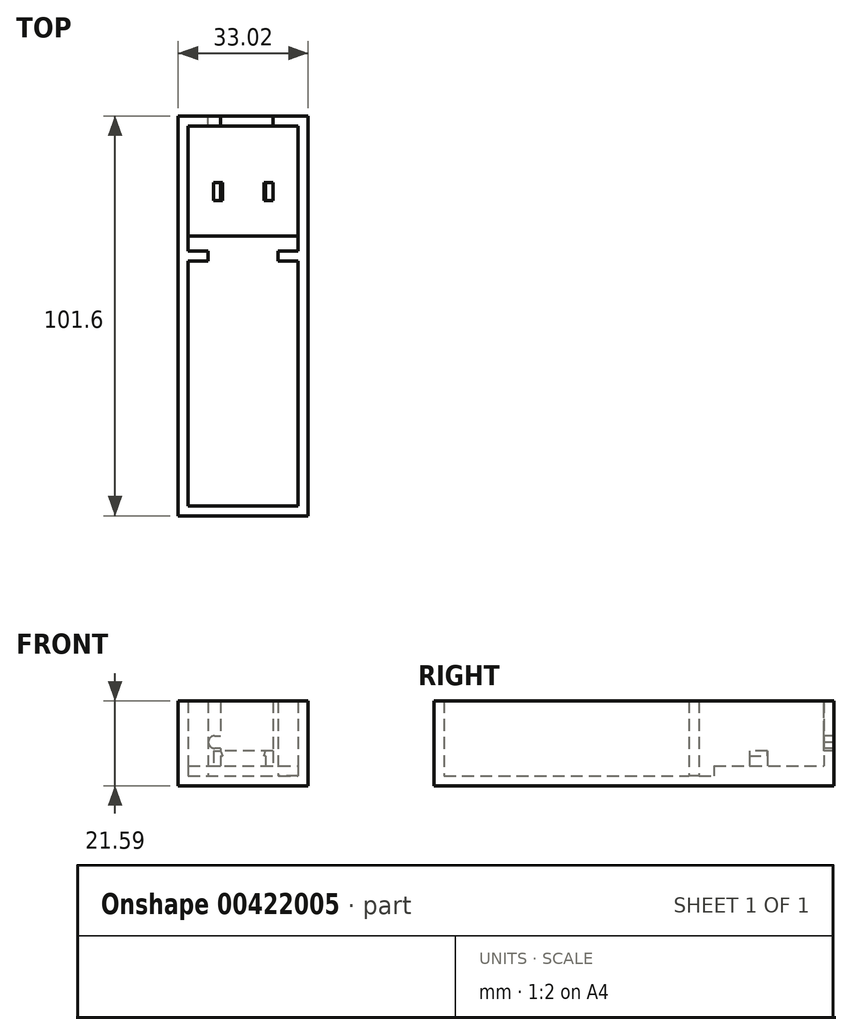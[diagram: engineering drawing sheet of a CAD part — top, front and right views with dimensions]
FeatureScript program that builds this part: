
annotation { "Feature Type Name" : "Feature", "Feature Type Description" : "" }
export const myFeature = defineFeature(function(context is Context, id is Id, definition is map)
    precondition{}
    {
        {
            var Q0;
            Q0=qCreatedBy(makeId("Top.planeOp"),FACE);
            var sketch = newSketch(context, id + "F0", { "sketchPlane" : qUnion([Q0])});
            skLineSegment(sketch, "E0.bottom", {"start": v(0, 0) * mm, "end": v(33.02, 0) * mm});
            skLineSegment(sketch, "E0.top", {"start": v(0, 101.6) * mm, "end": v(33.02, 101.6) * mm});
            skLineSegment(sketch, "E0.left", {"start": v(0, 0) * mm, "end": v(0, 101.6) * mm});
            skLineSegment(sketch, "E0.right", {"start": v(33.02, 0) * mm, "end": v(33.02, 101.6) * mm});
            skSolve(sketch);
        }
        {
            var Q0;
            Q0 = qSketchRegion(id + "F0", true);
            var Q1;
            Q1=makeQuery(id+"F0.imprint","IMPRINT",FACE,{"disambiguationData":[TD([[makeQuery(id+"F0.imprint","IMPRINT",EDGE,{"derivedFrom":sQuery(id+"F0.wireOp",EDGE,"E0.bottom")}),1.0]])]});
            extrude(context, id + "F1", {"entities" : qUnion([Q0, Q1]), "depth" : 2.54 * mm});
        }
        {
            var Q0;
            Q0=makeQuery(id+"F1.opExtrude","CAP_FACE",FACE,{"disambiguationData":[OSD([sQuery(id+"F0.wireOp",EDGE,"E0.bottom"),sQuery(id+"F0.wireOp",EDGE,"E0.top"),sQuery(id+"F0.wireOp",EDGE,"E0.left"),sQuery(id+"F0.wireOp",EDGE,"E0.right")])],"isStart":false});
            var sketch = newSketch(context, id + "F2", { "sketchPlane" : qUnion([Q0])});
            skLineSegment(sketch, "E1.bottom", {"start": v(2.54, 2.54) * mm, "end": v(30.48, 2.54) * mm});
            skLineSegment(sketch, "E1.top", {"start": v(2.54, 99.06) * mm, "end": v(30.48, 99.06) * mm});
            skLineSegment(sketch, "E1.left", {"start": v(2.54, 2.54) * mm, "end": v(2.54, 99.06) * mm});
            skLineSegment(sketch, "E1.right", {"start": v(30.48, 2.54) * mm, "end": v(30.48, 99.06) * mm});
            skLineSegment(sketch, "E2", {"start": v(2.54, 71.12) * mm, "end": v(30.48, 71.12) * mm});
            skLineSegment(sketch, "E3.bottom", {"start": v(22.22, 80.06) * mm, "end": v(24.05, 80.06) * mm});
            skLineSegment(sketch, "E3.top", {"start": v(22.22, 84.63) * mm, "end": v(24.05, 84.63) * mm});
            skLineSegment(sketch, "E3.left", {"start": v(22.22, 80.06) * mm, "end": v(22.22, 84.63) * mm});
            skLineSegment(sketch, "E3.right", {"start": v(24.05, 80.06) * mm, "end": v(24.05, 84.63) * mm});
            skLineSegment(sketch, "E4.bottom", {"start": v(8.97, 80.06) * mm, "end": v(10.8, 80.06) * mm});
            skLineSegment(sketch, "E4.top", {"start": v(8.97, 84.63) * mm, "end": v(10.8, 84.63) * mm});
            skLineSegment(sketch, "E4.left", {"start": v(10.8, 80.06) * mm, "end": v(10.8, 84.63) * mm});
            skLineSegment(sketch, "E4.right", {"start": v(8.97, 80.06) * mm, "end": v(8.97, 84.63) * mm});
            skLineSegment(sketch, "E5", {"start": v(16.51, 71.12) * mm, "end": v(16.5, 99.06) * mm, "construction": true});
            skLineSegment(sketch, "E6", {"start": v(22.22, 80.06) * mm, "end": v(16.5, 80.06) * mm, "construction": true});
            skLineSegment(sketch, "E7", {"start": v(16.5, 80.06) * mm, "end": v(10.8, 80.06) * mm, "construction": true});
            skLineSegment(sketch, "E8.bottom", {"start": v(2.54, 67.31) * mm, "end": v(7.62, 67.31) * mm});
            skLineSegment(sketch, "E8.top", {"start": v(2.54, 64.77) * mm, "end": v(7.62, 64.77) * mm});
            skLineSegment(sketch, "E8.left", {"start": v(2.54, 67.31) * mm, "end": v(2.54, 64.77) * mm});
            skLineSegment(sketch, "E8.right", {"start": v(7.62, 67.31) * mm, "end": v(7.62, 64.77) * mm});
            skLineSegment(sketch, "E9.bottom", {"start": v(30.48, 67.31) * mm, "end": v(25.4, 67.31) * mm});
            skLineSegment(sketch, "E9.top", {"start": v(30.48, 64.77) * mm, "end": v(25.4, 64.77) * mm});
            skLineSegment(sketch, "E9.left", {"start": v(30.48, 67.31) * mm, "end": v(30.48, 64.77) * mm});
            skLineSegment(sketch, "E9.right", {"start": v(25.4, 67.31) * mm, "end": v(25.4, 64.77) * mm});
            skSolve(sketch);
        }
        {
            var Q0;
            Q0=makeQuery(id+"F2.imprint","IMPRINT",FACE,{"disambiguationData":[TD([[makeQuery(id+"F2.imprint","IMPRINT",EDGE,{"derivedFrom":sQuery(id+"F2.wireOp",EDGE,"E1.bottom")}),-1.0]])]});
            var Q1;
            Q1=makeQuery(id+"F2.imprint","IMPRINT",FACE,{"disambiguationData":[TD([[makeQuery(id+"F2.imprint","IMPRINT",EDGE,{"derivedFrom":sQuery(id+"F2.wireOp",EDGE,"E8.bottom")}),-1.0]])]});
            var Q2;
            Q2=makeQuery(id+"F2.imprint","IMPRINT",FACE,{"disambiguationData":[TD([[makeQuery(id+"F2.imprint","IMPRINT",EDGE,{"derivedFrom":sQuery(id+"F2.wireOp",EDGE,"E9.bottom")}),1.0]])]});
            extrude(context, id + "F3", {"entities" : qUnion([Q0, Q1, Q2]), "operationType" : NewBodyOperationType.ADD, "depth" : 19.05 * mm});
        }
        {
            var Q0;
            {var subQ0=sQuery(id+"F2.wireOp",EDGE,"E1.top");Q0=makeQuery(id+"F2.imprint","IMPRINT",FACE,{"disambiguationData":[TD([[makeQuery(id+"F2.imprint","IMPRINT",EDGE,{"derivedFrom":subQ0}),-1.0]])]});}
            extrude(context, id + "F4", {"entities" : qUnion([Q0]), "operationType" : NewBodyOperationType.ADD, "depth" : 2.54 * mm});
        }
        {
            var Q0;
            Q0=makeQuery(id+"F2.imprint","IMPRINT",FACE,{"disambiguationData":[TD([[makeQuery(id+"F2.imprint","IMPRINT",EDGE,{"derivedFrom":sQuery(id+"F2.wireOp",EDGE,"E4.bottom")}),1.0]])]});
            var Q1;
            Q1=makeQuery(id+"F2.imprint","IMPRINT",FACE,{"disambiguationData":[TD([[makeQuery(id+"F2.imprint","IMPRINT",EDGE,{"derivedFrom":sQuery(id+"F2.wireOp",EDGE,"E3.bottom")}),1.0]])]});
            extrude(context, id + "F5", {"entities" : qUnion([Q0, Q1]), "operationType" : NewBodyOperationType.ADD, "depth" : 5.08 * mm});
        }
        {
            var Q0;
            Q0=makeQuery(id+"F4.opExtrude","CAP_FACE",FACE,{"disambiguationData":[OSD([sQuery(id+"F2.wireOp",EDGE,"E1.top"),sQuery(id+"F2.wireOp",EDGE,"E1.left"),sQuery(id+"F2.wireOp",EDGE,"E1.right"),sQuery(id+"F2.wireOp",EDGE,"E2"),sQuery(id+"F2.wireOp",EDGE,"E3.bottom"),sQuery(id+"F2.wireOp",EDGE,"E3.top"),sQuery(id+"F2.wireOp",EDGE,"E3.left"),sQuery(id+"F2.wireOp",EDGE,"E3.right"),sQuery(id+"F2.wireOp",EDGE,"E4.bottom"),sQuery(id+"F2.wireOp",EDGE,"E4.top"),sQuery(id+"F2.wireOp",EDGE,"E4.left"),sQuery(id+"F2.wireOp",EDGE,"E4.right")])],"isStart":false});
            var sketch = newSketch(context, id + "F6", { "sketchPlane" : qUnion([Q0])});
            skLineSegment(sketch, "E10", {"start": v(24.05, 84.63) * mm, "end": v(24.05, 99.06) * mm, "construction": true});
            skLineSegment(sketch, "E11", {"start": v(10.8, 84.63) * mm, "end": v(10.8, 99.06) * mm, "construction": true});
            skSolve(sketch);
        }
        {
            var Q0;
            Q0=makeQuery(id+"F3.opExtrude","SWEPT_FACE",FACE,{"disambiguationData":[OSD([sQuery(id+"F2.wireOp",EDGE,"E1.top")])]});
            var sketch = newSketch(context, id + "F7", { "sketchPlane" : qUnion([Q0])});
            skLineSegment(sketch, "E12.bottom", {"start": v(10.8, 8.9) * mm, "end": v(24.05, 8.9) * mm});
            skLineSegment(sketch, "E12.top", {"start": v(10.8, 21.59) * mm, "end": v(24.05, 21.59) * mm});
            skLineSegment(sketch, "E12.left", {"start": v(10.8, 8.9) * mm, "end": v(10.8, 21.59) * mm});
            skLineSegment(sketch, "E12.right", {"start": v(24.05, 8.9) * mm, "end": v(24.05, 21.59) * mm});
            skLineSegment(sketch, "E13", {"start": v(24.05, 8.9) * mm, "end": v(24.05, 5.08) * mm, "construction": true});
            skLineSegment(sketch, "E14", {"start": v(10.8, 8.9) * mm, "end": v(10.8, 5.08) * mm, "construction": true});
            skLineSegment(sketch, "E15", {"start": v(10.8, 12.7) * mm, "end": v(7.64, 12.7) * mm});
            skLineSegment(sketch, "E16", {"start": v(7.64, 12.7) * mm, "end": v(7.64, 9.53) * mm});
            skLineSegment(sketch, "E17", {"start": v(7.64, 9.53) * mm, "end": v(10.8, 9.53) * mm});
            skSolve(sketch);
        }
        {
            var Q0;
            Q0=makeQuery(id+"F7.imprint","IMPRINT",FACE,{"disambiguationData":[TD([[makeQuery(id+"F7.imprint","IMPRINT",EDGE,{"derivedFrom":sQuery(id+"F7.wireOp",EDGE,"E12.bottom")}),1.0]])]});
            var Q1;
            {var subQ0=sQuery(id+"F7.wireOp",EDGE,"E15");Q1=makeQuery(id+"F7.imprint","IMPRINT",FACE,{"disambiguationData":[TD([[makeQuery(id+"F7.imprint","IMPRINT",EDGE,{"derivedFrom":subQ0}),1.0]])]});}
            extrude(context, id + "F8", {"entities" : qUnion([Q0, Q1]), "operationType" : NewBodyOperationType.REMOVE, "oppositeDirection" : true, "depth" : 25.4 * mm});
        }
        {
            var Q0;
            Q0=makeQuery(id+"F8.boolean.opBoolean","COPY",EDGE,{"derivedFrom":makeQuery(id+"F8.opExtrude","SWEPT_EDGE",EDGE,{"disambiguationData":[OSD([sQuery(id+"F7.wireOp",EDGE,"E15"),sQuery(id+"F7.wireOp",EDGE,"E16")])]})});
            var Q1;
            Q1=makeQuery(id+"F8.boolean.opBoolean","COPY",EDGE,{"derivedFrom":makeQuery(id+"F8.opExtrude","SWEPT_EDGE",EDGE,{"disambiguationData":[OSD([sQuery(id+"F7.wireOp",EDGE,"E16"),sQuery(id+"F7.wireOp",EDGE,"E17")])]})});
            fillet(context, id + "F9", {"entities" : qUnion([Q0, Q1]), "radius" : 1.65 * mm, "tangentPropagation" : true, "allowEdgeOverflow" : false});
        }
        {
            var Q0;
            Q0=makeQuery(id+"F5.opExtrude","CAP_FACE",FACE,{"disambiguationData":[OSD([sQuery(id+"F2.wireOp",EDGE,"E4.bottom"),sQuery(id+"F2.wireOp",EDGE,"E4.top"),sQuery(id+"F2.wireOp",EDGE,"E4.left"),sQuery(id+"F2.wireOp",EDGE,"E4.right")])],"isStart":false});
            var sketch = newSketch(context, id + "F10", { "sketchPlane" : qUnion([Q0])});
            skLineSegment(sketch, "E18.bottom", {"start": v(8.97, 80.06) * mm, "end": v(11.25, 80.06) * mm});
            skLineSegment(sketch, "E18.top", {"start": v(8.97, 84.63) * mm, "end": v(11.25, 84.63) * mm});
            skLineSegment(sketch, "E18.left", {"start": v(8.97, 80.06) * mm, "end": v(8.97, 84.63) * mm});
            skLineSegment(sketch, "E18.right", {"start": v(11.25, 80.06) * mm, "end": v(11.25, 84.63) * mm});
            skLineSegment(sketch, "E19.bottom", {"start": v(24.05, 80.06) * mm, "end": v(21.77, 80.06) * mm});
            skLineSegment(sketch, "E19.top", {"start": v(24.05, 84.63) * mm, "end": v(21.77, 84.63) * mm});
            skLineSegment(sketch, "E19.left", {"start": v(24.05, 80.06) * mm, "end": v(24.05, 84.63) * mm});
            skLineSegment(sketch, "E19.right", {"start": v(21.77, 80.06) * mm, "end": v(21.77, 84.63) * mm});
            skSolve(sketch);
        }
        {
            var Q0;
            {var subQ2=sQuery(id+"F10.wireOp",EDGE,"E18.right");Q0=makeQuery(id+"F10.imprint","IMPRINT",FACE,{"disambiguationData":[TD([[makeQuery(id+"F10.imprint","IMPRINT",EDGE,{"derivedFrom":subQ2}),1.0]])]});}
            var Q1;
            {var subQ0=sQuery(id+"F10.wireOp",EDGE,"E18.left");Q1=makeQuery(id+"F10.imprint","IMPRINT",FACE,{"disambiguationData":[TD([[makeQuery(id+"F10.imprint","IMPRINT",EDGE,{"derivedFrom":subQ0}),-1.0]])]});}
            var Q2;
            Q2=makeQuery(id+"F10.imprint","IMPRINT",FACE,{"disambiguationData":[TD([[makeQuery(id+"F10.imprint","IMPRINT",EDGE,{"derivedFrom":sQuery(id+"F10.wireOp",EDGE,"E19.bottom")}),-1.0]])]});
            extrude(context, id + "F11", {"entities" : qUnion([Q0, Q1, Q2]), "operationType" : NewBodyOperationType.ADD, "depth" : 1.27 * mm});
        }
        {
            var Q0;
            Q0=makeQuery(id+"F11.boolean.opBoolean","MERGE",FACE,{"derivedFrom":[makeQuery(id+"F5.opExtrude","SWEPT_FACE",FACE,{"disambiguationData":[OSD([sQuery(id+"F2.wireOp",EDGE,"E4.bottom")])]}),makeQuery(id+"F11.opExtrude","SWEPT_FACE",FACE,{"disambiguationData":[OSD([sQuery(id+"F10.wireOp",EDGE,"E18.bottom")])]})]});
            var sketch = newSketch(context, id + "F12", { "sketchPlane" : qUnion([Q0])});
            skLineSegment(sketch, "E20", {"start": v(10.8, 7.62) * mm, "end": v(10.8, 8.9) * mm, "construction": true});
            skLineSegment(sketch, "E21", {"start": v(22.22, 7.62) * mm, "end": v(22.22, 8.9) * mm, "construction": true});
            skLineSegment(sketch, "E22", {"start": v(11.25, 7.62) * mm, "end": v(10.8, 8.9) * mm});
            skLineSegment(sketch, "E23", {"start": v(22.22, 8.9) * mm, "end": v(21.77, 7.62) * mm});
            skLineSegment(sketch, "E24", {"start": v(22.22, 8.9) * mm, "end": v(21.77, 8.9) * mm});
            skLineSegment(sketch, "E25", {"start": v(21.77, 8.9) * mm, "end": v(21.77, 7.62) * mm});
            skSolve(sketch);
        }
        {
            var Q0;
            {var subQ0=sQuery(id+"F12.wireOp",EDGE,"E22");Q0=makeQuery(id+"F12.imprint","IMPRINT",FACE,{"disambiguationData":[TD([[makeQuery(id+"F12.imprint","IMPRINT",EDGE,{"derivedFrom":subQ0}),-1.0]])]});}
            var Q1;
            Q1=makeQuery(id+"F12.imprint","IMPRINT",FACE,{"disambiguationData":[TD([[makeQuery(id+"F12.imprint","IMPRINT",EDGE,{"derivedFrom":sQuery(id+"F12.wireOp",EDGE,"E23")}),-1.0]])]});
            extrude(context, id + "F13", {"entities" : qUnion([Q0, Q1]), "operationType" : NewBodyOperationType.REMOVE, "oppositeDirection" : true, "depth" : 6.35 * mm});
        }
    });
